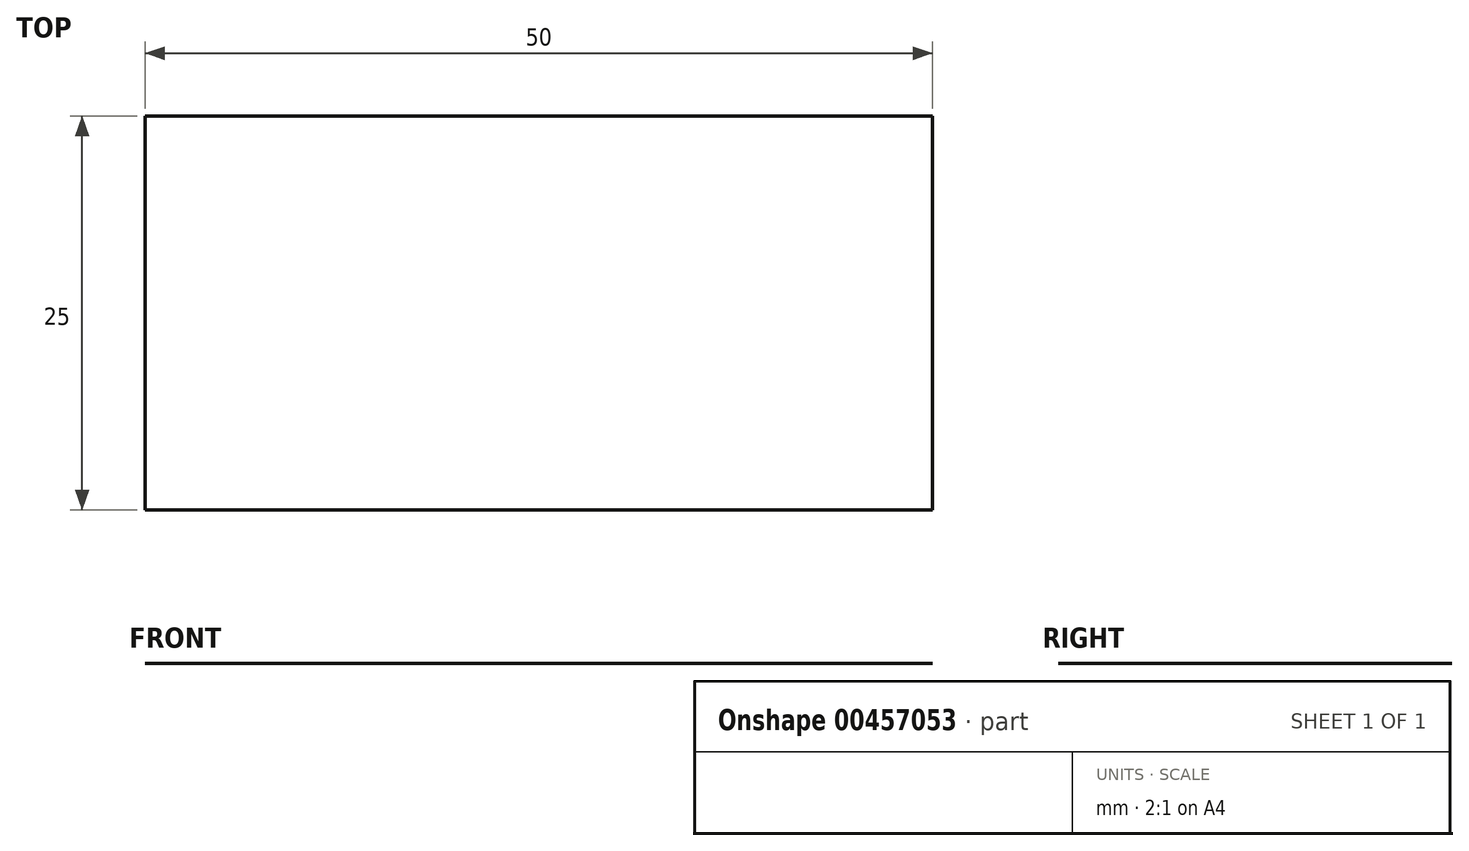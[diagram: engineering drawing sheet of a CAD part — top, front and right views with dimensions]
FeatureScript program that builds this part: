
annotation { "Feature Type Name" : "Feature", "Feature Type Description" : "" }
export const myFeature = defineFeature(function(context is Context, id is Id, definition is map)
    precondition{}
    {
        {
            var Q0;
            Q0=qCreatedBy(makeId("Front.planeOp"),FACE);
            var sketch = newSketch(context, id + "F0", { "sketchPlane" : qUnion([Q0])});
            skLineSegment(sketch, "E0", {"start": v(0, 0) * mm, "end": v(50, 0) * mm});
            skLineSegment(sketch, "E1", {"start": v(50, 0) * mm, "end": v(67.32, 10) * mm});
            skLineSegment(sketch, "E2", {"start": v(0, 0) * mm, "end": v(0, 10) * mm});
            skSolve(sketch);
        }
        {
            var Q0;
            Q0 = qSketchRegion(id + "F0", true);
            var Q1;
            Q1=sQuery(id+"F0.wireOp",EDGE,"E0");
            extrude(context, id + "F1", {"entities" : qUnion([Q0]), "bodyType" : ToolBodyType.SURFACE, "surfaceEntities" : qUnion([Q1]), "depth" : 25 * mm});
        }
    });
